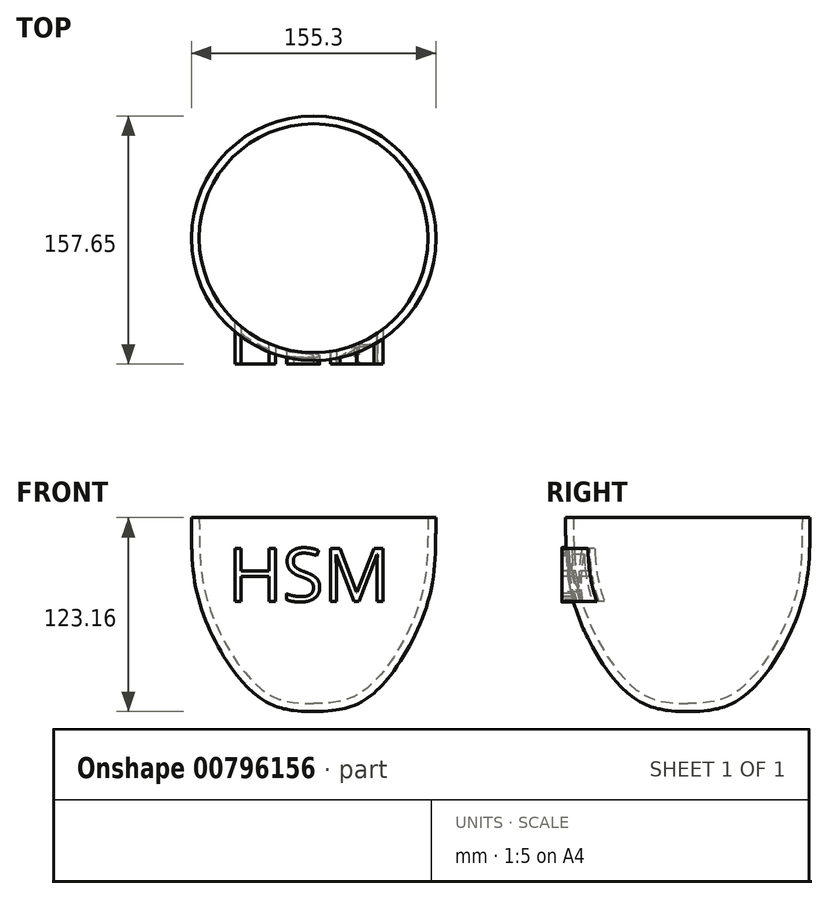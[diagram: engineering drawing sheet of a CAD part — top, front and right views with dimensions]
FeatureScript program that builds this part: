
annotation { "Feature Type Name" : "Feature", "Feature Type Description" : "" }
export const myFeature = defineFeature(function(context is Context, id is Id, definition is map)
    precondition{}
    {
        {
            var Q0;
            Q0=qCreatedBy(makeId("Front.planeOp"),FACE);
            var sketch = newSketch(context, id + "F0", { "sketchPlane" : qUnion([Q0])});
            skLineSegment(sketch, "E0", {"start": v(0, 69.84) * mm, "end": v(0, -73) * mm});
            skFitSpline(sketch, "E1", {"points": [v(72.83, 58.73) * mm, v(68.61, 4.2) * mm, v(41.34, -48.08) * mm, v(18.53, -63.13) * mm, v(-10.09, -64.93) * mm], "startDerivative": vector(-6.95, -187) * mm, "endDerivative": vector(-142.94, 0.54) * mm});
            skFitSpline(sketch, "E2.0", {"points": [v(77.83, 58.54) * mm, v(77.69, 54.72) * mm, v(77.58, 47.03) * mm, v(77.49, 37.22) * mm, v(77.19, 29.23) * mm, v(76.8, 23.16) * mm, v(76.15, 17) * mm, v(75.2, 10.75) * mm, v(74.1, 5.46) * mm, v(73, 1.2) * mm, v(71.77, -3.08) * mm, v(69.97, -8.42) * mm, v(67.47, -14.74) * mm, v(64.68, -20.94) * mm, v(61.64, -26.95) * mm, v(58.41, -32.73) * mm, v(55.02, -38.2) * mm, v(51.53, -43.32) * mm, v(47.97, -48.03) * mm, v(44.38, -52.27) * mm, v(40.78, -56) * mm, v(37.1, -59.26) * mm, v(33.33, -62.04) * mm, v(29.43, -64.37) * mm, v(25.37, -66.24) * mm, v(21.87, -67.44) * mm, v(18.99, -68.19) * mm, v(16.07, -68.8) * mm, v(12.38, -69.36) * mm, v(6.4, -69.88) * mm, v(-1.16, -70.02) * mm, v(-7.16, -69.94) * mm, v(-10.1, -69.93) * mm]});
            skLineSegment(sketch, "E3", {"start": v(66.84, 53.14) * mm, "end": v(92.49, 53.14) * mm});
            skPoint(sketch, "E4.visualSharp", {"position": v(119.31, 14.18) * mm});
            skPoint(sketch, "E5.visualSharp", {"position": v(119.31, -47.63) * mm});
            skPoint(sketch, "E6.visualSharp", {"position": v(119.31, 0) * mm});
            skFitSpline(sketch, "E7", {"points": [v(77.23, 30.63) * mm, v(114.84, 40.6) * mm, v(126.95, -10.15) * mm, v(48.7, -47) * mm], "startDerivative": vector(149.47, 88.4) * mm, "endDerivative": vector(-252.23, -53.69) * mm});
            skLineSegment(sketch, "E8", {"start": v(77.23, 30.63) * mm, "end": v(73.68, 28.34) * mm});
            skSolve(sketch);
        }
        {
            var Q0;
            {var subQ0=sQuery(id+"F0.wireOp",EDGE,"E1");var subQ1=sQuery(id+"F0.wireOp",EDGE,"E0");var subQ2=makeQuery(id+"F0.imprint","INTERSECT",VERTEX,{"derivedFrom":[subQ1,subQ0]});Q0=makeQuery(id+"F0.imprint","IMPRINT",FACE,{"disambiguationData":[TD([[makeQuery(id+"F0.imprint","IMPRINT",EDGE,{"disambiguationData":[TD([[subQ2,-1.0]])],"derivedFrom":subQ1}),1.0]])]});}
            var Q1;
            {var subQ0=sQuery(id+"F0.wireOp",EDGE,"JhlxOL22-MIaC-4HUc-FV5r-gj2OHG0Cgbx8");var subQ1=sQuery(id+"F0.wireOp",EDGE,"E1");var subQ2=makeQuery(id+"F0.imprint","INTERSECT",VERTEX,{"derivedFrom":[subQ1,subQ0]});Q1=makeQuery(id+"F0.imprint","IMPRINT",FACE,{"disambiguationData":[TD([[makeQuery(id+"F0.imprint","IMPRINT",EDGE,{"disambiguationData":[TD([[subQ2,-1.0]])],"derivedFrom":subQ1}),1.0]])]});}
            var Q2;
            {var subQ0=sQuery(id+"F0.wireOp",EDGE,"JhlxOL22-MIaC-4HUc-FV5r-gj2OHG0Cgbx8");var subQ1=sQuery(id+"F0.wireOp",EDGE,"E1");var subQ2=makeQuery(id+"F0.imprint","INTERSECT",VERTEX,{"derivedFrom":[subQ1,subQ0]});Q2=makeQuery(id+"F0.imprint","IMPRINT",FACE,{"disambiguationData":[TD([[makeQuery(id+"F0.imprint","IMPRINT",EDGE,{"disambiguationData":[TD([[subQ2,1.0]])],"derivedFrom":subQ1}),1.0]])]});}
            var Q3;
            Q3=sQuery(id+"F0.wireOp",EDGE,"E0");
            revolve(context, id + "F1", {"surfaceOperationType" : NewSurfaceOperationType.NEW, "entities" : qUnion([Q0, Q1, Q2]), "axis" : qUnion([Q3]), "revolveType" : RevolveType.FULL});
        }
        {
            var Q0;
            Q0=qCreatedBy(makeId("Front.planeOp"),FACE);
            cPlane(context, id + "F2", {"entities" : qUnion([Q0]), "cplaneType" : CPlaneType.OFFSET, "offset" : 80 * mm, "width" : 150 * mm, "height" : 150 * mm});
        }
        {
            var Q0;
            Q0=qCreatedBy(id+"F2.planeOp",FACE);
            var sketch = newSketch(context, id + "F3", { "sketchPlane" : qUnion([Q0])});
            skText(sketch, "E9", { "text": "HSM", "fontName": "OpenSans-Regular.ttf"});
            const initialGuessF3  = {"E9": [-0.05452, 0, 1, 0, 0.03395]};
            skSetInitialGuess(sketch, initialGuessF3);
            skSolve(sketch);
        }
        {
            var Q0;
            Q0 = qSketchRegion(id + "F3", true);
            extrude(context, id + "F4", {"entities" : qUnion([Q0]), "operationType" : NewBodyOperationType.ADD, "endBound" : BoundingType.UP_TO_NEXT, "oppositeDirection" : true, "depth" : 25 * mm, "offsetDistance" : 25 * mm});
        }
        {
            var Q0;
            Q0=qCreatedBy(makeId("Right.planeOp"),FACE);
            cPlane(context, id + "F5", {"entities" : qUnion([Q0]), "cplaneType" : CPlaneType.OFFSET, "offset" : 75 * mm, "width" : 150 * mm, "height" : 150 * mm});
        }
        {
            var Q0;
            Q0=qCreatedBy(id+"F5.planeOp",FACE);
            var sketch = newSketch(context, id + "F6", { "sketchPlane" : qUnion([Q0])});
            skCircle(sketch, "E10", {"center": v(0, 28.25) * mm, "radius": 5.44 * mm});
            skSolve(sketch);
        }
        {
            var Q0;
            Q0=qCreatedBy(makeId("Top.planeOp"),FACE);
            cPlane(context, id + "F7", {"entities" : qUnion([Q0]), "cplaneType" : CPlaneType.OFFSET, "offset" : 70 * mm, "oppositeDirection" : true, "width" : 150 * mm, "height" : 150 * mm});
        }
        {
            var Q0;
            Q0=qCreatedBy(id+"F7.planeOp",FACE);
            var sketch = newSketch(context, id + "F8", { "sketchPlane" : qUnion([Q0])});
            skCircle(sketch, "E11", {"center": v(0, 0) * mm, "radius": 38.35 * mm});
            skSolve(sketch);
        }
        {
            var Q0;
            Q0=sQuery(id+"F8.wireOp",EDGE,"E11");
            extrude(context, id + "F9", {"bodyType" : ToolBodyType.SURFACE, "surfaceEntities" : qUnion([Q0]), "endBound" : BoundingType.UP_TO_NEXT, "depth" : 25 * mm, "offsetDistance" : 25 * mm});
        }
    });
